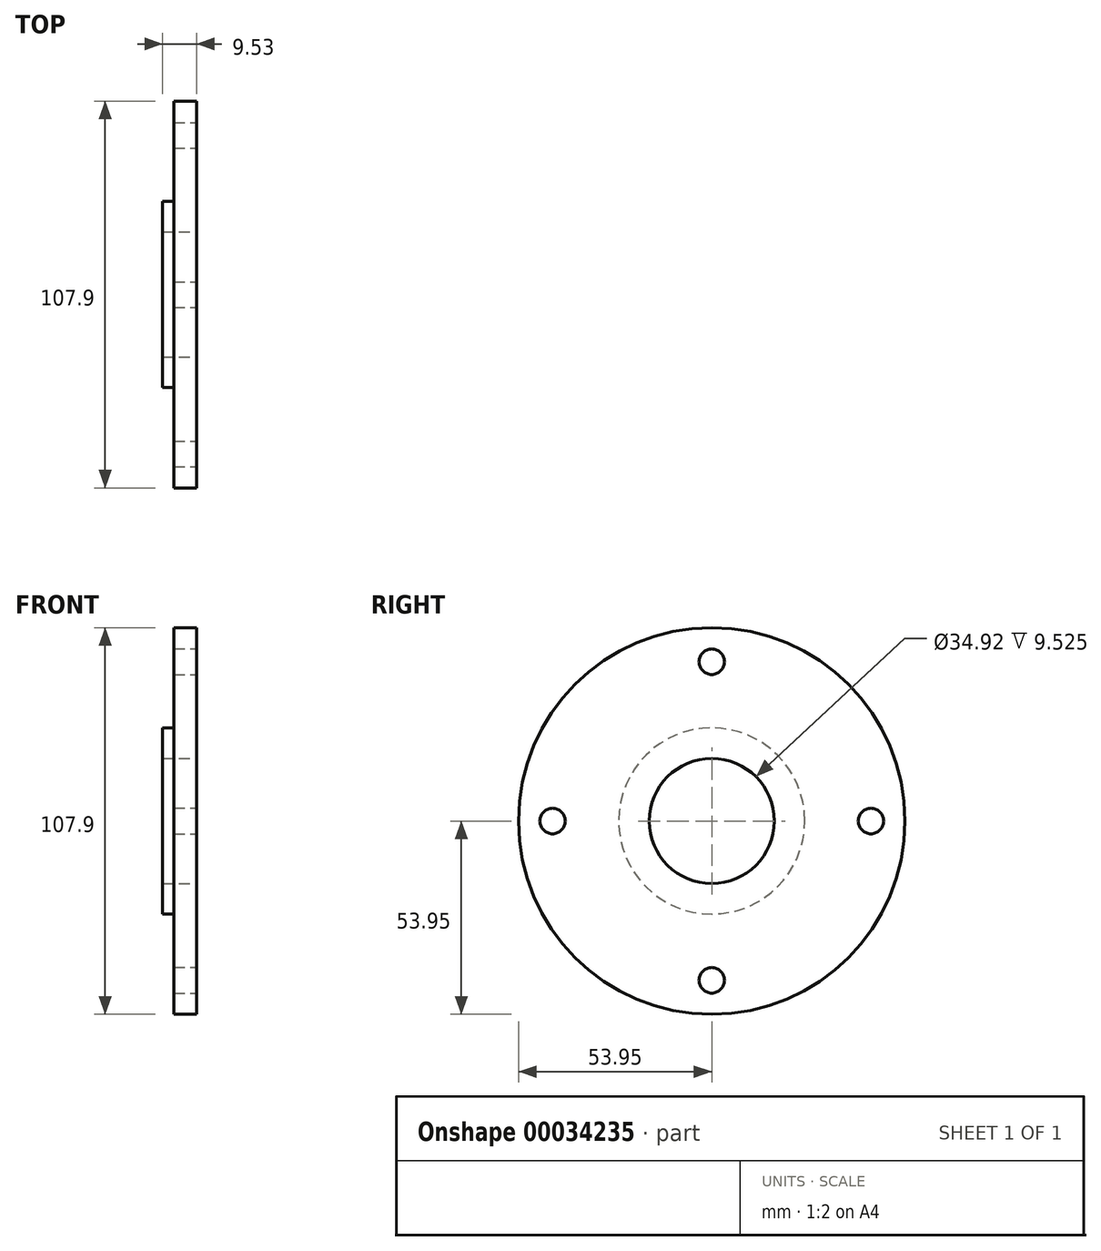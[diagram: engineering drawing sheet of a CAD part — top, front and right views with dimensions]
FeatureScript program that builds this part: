
annotation { "Feature Type Name" : "Feature", "Feature Type Description" : "" }
export const myFeature = defineFeature(function(context is Context, id is Id, definition is map)
    precondition{}
    {
        {
            var Q0;
            Q0=qCreatedBy(makeId("Right.planeOp"),FACE);
            var sketch = newSketch(context, id + "F0", { "sketchPlane" : qUnion([Q0])});
            skCircle(sketch, "E0", {"center": v(0, 0) * mm, "radius": 53.95 * mm});
            skSolve(sketch);
        }
        {
            var Q0;
            Q0 = qSketchRegion(id + "F0", true);
            extrude(context, id + "F1", {"entities" : qUnion([Q0]), "oppositeDirection" : true, "depth" : 6.35 * mm});
        }
        {
            var Q0;
            Q0=makeQuery(id+"F1.opExtrude","CAP_FACE",FACE,{"disambiguationData":[OSD([sQuery(id+"F0.wireOp",EDGE,"E0")])],"isStart":false});
            var sketch = newSketch(context, id + "F2", { "sketchPlane" : qUnion([Q0])});
            skCircle(sketch, "E1", {"center": v(0, 0) * mm, "radius": 25.97 * mm});
            skSolve(sketch);
        }
        {
            var Q0;
            Q0 = qSketchRegion(id + "F2", true);
            extrude(context, id + "F3", {"entities" : qUnion([Q0]), "operationType" : NewBodyOperationType.ADD, "depth" : 3.17 * mm});
        }
        {
            var Q0;
            Q0=makeQuery(id+"F1.opExtrude","CAP_FACE",FACE,{"disambiguationData":[OSD([sQuery(id+"F0.wireOp",EDGE,"E0")])],"isStart":true});
            var sketch = newSketch(context, id + "F4", { "sketchPlane" : qUnion([Q0])});
            skCircle(sketch, "E2", {"center": v(0, 0) * mm, "radius": 17.46 * mm});
            skPoint(sketch, "E3", {"position": v(0, -44.45) * mm});
            skPoint(sketch, "E4.1.0", {"position": v(44.45, 0) * mm});
            skPoint(sketch, "E4.2.0", {"position": v(0, 44.45) * mm});
            skPoint(sketch, "E4.3.0", {"position": v(-44.45, 0) * mm});
            skSolve(sketch);
        }
        {
            var Q0;
            Q0 = qSketchRegion(id + "F4", true);
            extrude(context, id + "F5", {"entities" : qUnion([Q0]), "operationType" : NewBodyOperationType.REMOVE, "endBound" : BoundingType.THROUGH_ALL, "oppositeDirection" : true, "depth" : 25.4 * mm});
        }
        {
            var Q0;
            Q0=sQuery(id+"F4.wireOp",VERTEX,"E3");
            var Q1;
            Q1=sQuery(id+"F4.wireOp",VERTEX,"E4.1.0");
            var Q2;
            Q2=sQuery(id+"F4.wireOp",VERTEX,"E4.2.0");
            var Q3;
            Q3=sQuery(id+"F4.wireOp",VERTEX,"E4.3.0");
            var Q4;
            Q4=makeQuery(id+"F1.opExtrude","SWEPT_BODY",BODY,{"disambiguationData":[OSD([sQuery(id+"F0.wireOp",EDGE,"E0")])]});
            hole(context, id + "F6", {"style" : HoleStyle.SIMPLE, "holeDiameter" : 7.14 * mm, "endStyle" : HoleEndStyle.THROUGH, "locations" : qUnion([Q0, Q1, Q2, Q3]), "scope" : qUnion([Q4])});
        }
    });
